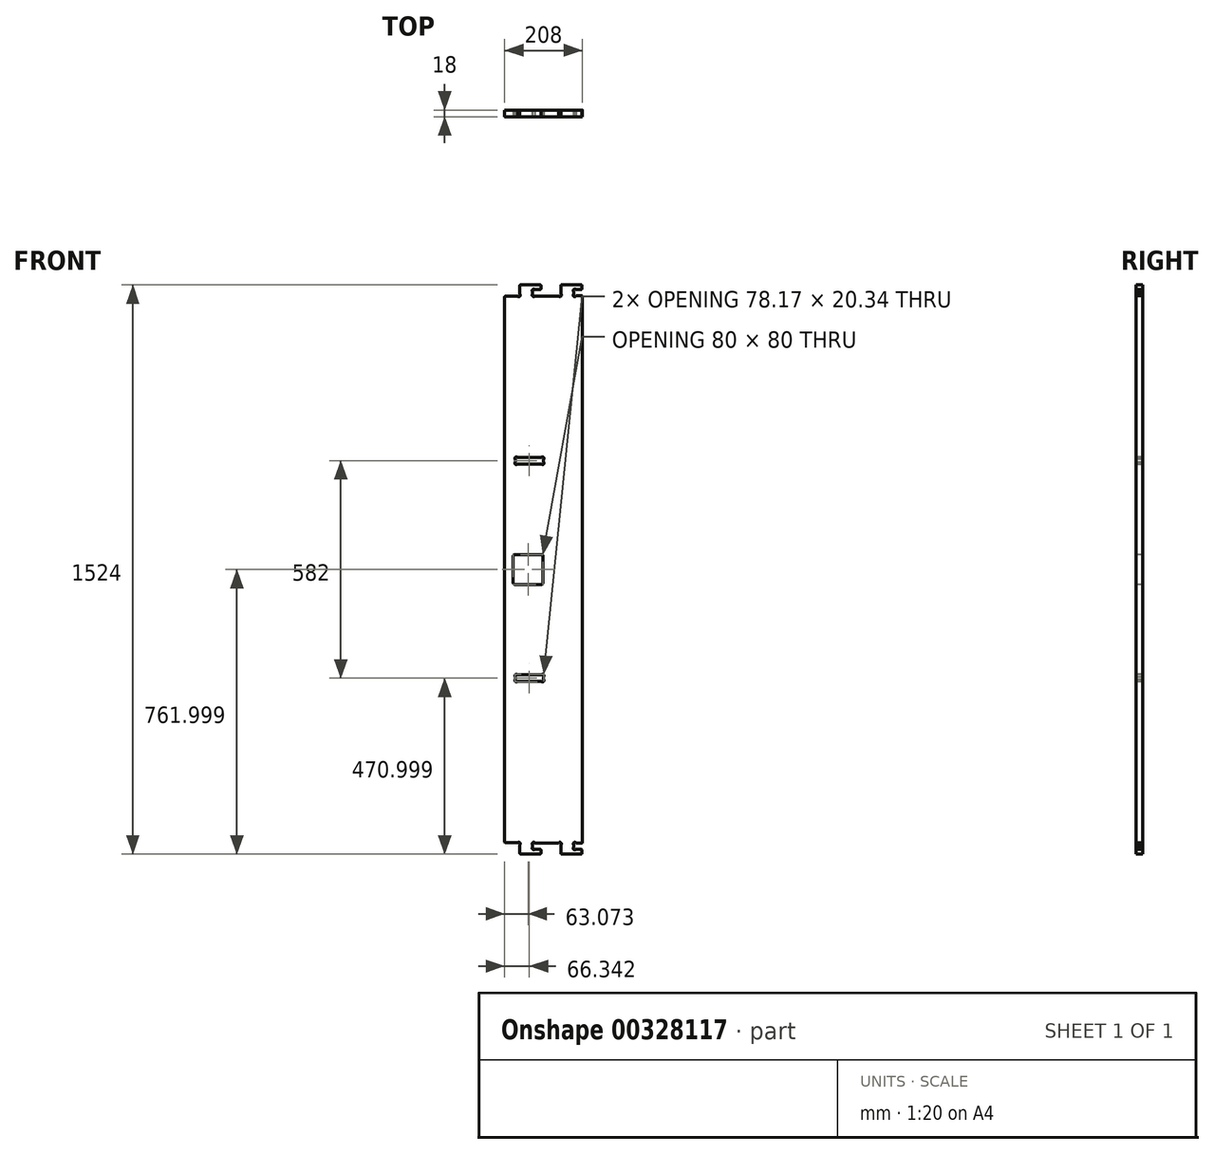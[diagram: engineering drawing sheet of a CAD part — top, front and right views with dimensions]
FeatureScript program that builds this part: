
annotation { "Feature Type Name" : "Feature", "Feature Type Description" : "" }
export const myFeature = defineFeature(function(context is Context, id is Id, definition is map)
    precondition{}
    {
        {
            var Q0;
            Q0=qCreatedBy(makeId("Front.planeOp"),FACE);
            var sketch = newSketch(context, id + "F0", { "sketchPlane" : qUnion([Q0])});
            skArc(sketch, "E0", {"start": v(-163.49, 53.85) * mm, "mid": v(-162.32, 56.68) * mm, "end": v(-159.49, 57.85) * mm});
            skLineSegment(sketch, "E1", {"start": v(-159.49, 57.85) * mm, "end": v(-87.49, 57.85) * mm});
            skArc(sketch, "E2", {"start": v(-87.49, 57.85) * mm, "mid": v(-84.66, 56.68) * mm, "end": v(-83.49, 53.85) * mm});
            skLineSegment(sketch, "E3", {"start": v(-83.49, 53.85) * mm, "end": v(-83.49, -18.15) * mm});
            skArc(sketch, "E4", {"start": v(-83.49, -18.15) * mm, "mid": v(-84.66, -20.98) * mm, "end": v(-87.49, -22.15) * mm});
            skLineSegment(sketch, "E5", {"start": v(-87.49, -22.15) * mm, "end": v(-159.49, -22.15) * mm});
            skArc(sketch, "E6", {"start": v(-159.49, -22.15) * mm, "mid": v(-162.32, -20.98) * mm, "end": v(-163.49, -18.15) * mm});
            skLineSegment(sketch, "E7", {"start": v(-163.49, -18.15) * mm, "end": v(-163.49, 53.85) * mm});
            skArc(sketch, "E8", {"start": v(-87.96, -282.15) * mm, "mid": v(-82.3, -282.15) * mm, "end": v(-82.3, -276.5) * mm});
            skLineSegment(sketch, "E9", {"start": v(-82.3, -276.5) * mm, "end": v(-82.3, -269.8) * mm});
            skArc(sketch, "E10", {"start": v(-82.3, -269.8) * mm, "mid": v(-82.3, -264.15) * mm, "end": v(-87.96, -264.15) * mm});
            skLineSegment(sketch, "E11", {"start": v(-87.96, -264.15) * mm, "end": v(-152.48, -264.15) * mm});
            skArc(sketch, "E12", {"start": v(-152.48, -264.15) * mm, "mid": v(-158.13, -264.15) * mm, "end": v(-158.13, -269.8) * mm});
            skLineSegment(sketch, "E13", {"start": v(-158.13, -269.8) * mm, "end": v(-158.13, -276.5) * mm});
            skArc(sketch, "E14", {"start": v(-158.13, -276.5) * mm, "mid": v(-158.13, -282.15) * mm, "end": v(-152.48, -282.15) * mm});
            skLineSegment(sketch, "E15", {"start": v(-152.48, -282.15) * mm, "end": v(-87.96, -282.15) * mm});
            skLineSegment(sketch, "E16", {"start": v(-82.3, 305.5) * mm, "end": v(-82.3, 312.2) * mm});
            skArc(sketch, "E17", {"start": v(-82.3, 312.2) * mm, "mid": v(-82.3, 317.85) * mm, "end": v(-87.96, 317.85) * mm});
            skLineSegment(sketch, "E18", {"start": v(-87.96, 317.85) * mm, "end": v(-152.48, 317.85) * mm});
            skArc(sketch, "E19", {"start": v(-152.48, 317.85) * mm, "mid": v(-158.13, 317.85) * mm, "end": v(-158.13, 312.2) * mm});
            skLineSegment(sketch, "E20", {"start": v(-158.13, 312.2) * mm, "end": v(-158.13, 305.5) * mm});
            skArc(sketch, "E21", {"start": v(-158.13, 305.5) * mm, "mid": v(-158.13, 299.85) * mm, "end": v(-152.48, 299.85) * mm});
            skLineSegment(sketch, "E22", {"start": v(-152.48, 299.85) * mm, "end": v(-87.96, 299.85) * mm});
            skArc(sketch, "E23", {"start": v(-87.96, 299.85) * mm, "mid": v(-82.3, 299.85) * mm, "end": v(-82.3, 305.5) * mm});
            skLineSegment(sketch, "E24", {"start": v(-105.9, -713.65) * mm, "end": v(-105.29, -714.15) * mm});
            skLineSegment(sketch, "E25", {"start": v(-105.29, -714.15) * mm, "end": v(-41.96, -714.15) * mm});
            skLineSegment(sketch, "E26", {"start": v(-41.96, -714.15) * mm, "end": v(-41.47, -713.65) * mm});
            skArc(sketch, "E27", {"start": v(-41.47, -713.65) * mm, "mid": v(-35.81, -713.65) * mm, "end": v(-35.81, -719.3) * mm});
            skLineSegment(sketch, "E28", {"start": v(-35.81, -719.3) * mm, "end": v(-35.8, -742.15) * mm});
            skArc(sketch, "E29", {"start": v(-35.8, -742.15) * mm, "mid": v(-35.22, -743.57) * mm, "end": v(-33.8, -744.15) * mm});
            skLineSegment(sketch, "E30", {"start": v(-33.8, -744.15) * mm, "end": v(18.44, -744.15) * mm});
            skArc(sketch, "E31", {"start": v(18.44, -744.15) * mm, "mid": v(19.85, -743.56) * mm, "end": v(20.44, -742.15) * mm});
            skLineSegment(sketch, "E32", {"start": v(20.44, -742.15) * mm, "end": v(20.44, -733.65) * mm});
            skArc(sketch, "E33", {"start": v(20.44, -733.65) * mm, "mid": v(19.85, -732.24) * mm, "end": v(18.44, -731.65) * mm});
            skLineSegment(sketch, "E34", {"start": v(18.44, -731.65) * mm, "end": v(4.1, -731.65) * mm});
            skArc(sketch, "E35", {"start": v(4.1, -731.65) * mm, "mid": v(-1.56, -731.65) * mm, "end": v(-1.56, -726) * mm});
            skLineSegment(sketch, "E36", {"start": v(-1.56, -726) * mm, "end": v(-1.56, -719.3) * mm});
            skArc(sketch, "E37", {"start": v(-1.56, -719.3) * mm, "mid": v(-1.56, -713.65) * mm, "end": v(4.1, -713.65) * mm});
            skLineSegment(sketch, "E38", {"start": v(4.1, -713.65) * mm, "end": v(5.07, -714.65) * mm});
            skLineSegment(sketch, "E39", {"start": v(5.07, -714.65) * mm, "end": v(20.44, -714.65) * mm});
            skArc(sketch, "E40", {"start": v(20.44, -714.65) * mm, "mid": v(21.14, -714.36) * mm, "end": v(21.44, -713.65) * mm});
            skLineSegment(sketch, "E41", {"start": v(21.44, -713.65) * mm, "end": v(21.44, 749.35) * mm});
            skArc(sketch, "E42", {"start": v(21.44, 749.35) * mm, "mid": v(21.14, 750.06) * mm, "end": v(20.44, 750.35) * mm});
            skLineSegment(sketch, "E43", {"start": v(20.44, 750.35) * mm, "end": v(5.12, 750.35) * mm});
            skLineSegment(sketch, "E44", {"start": v(5.12, 750.35) * mm, "end": v(4.1, 749.35) * mm});
            skArc(sketch, "E45", {"start": v(4.1, 749.35) * mm, "mid": v(-1.56, 749.35) * mm, "end": v(-1.56, 755) * mm});
            skLineSegment(sketch, "E46", {"start": v(-1.56, 755) * mm, "end": v(-1.56, 761.7) * mm});
            skArc(sketch, "E47", {"start": v(-1.56, 761.7) * mm, "mid": v(-1.56, 767.35) * mm, "end": v(4.1, 767.35) * mm});
            skLineSegment(sketch, "E48", {"start": v(4.1, 767.35) * mm, "end": v(18.44, 767.35) * mm});
            skArc(sketch, "E49", {"start": v(18.44, 767.35) * mm, "mid": v(19.85, 767.94) * mm, "end": v(20.44, 769.35) * mm});
            skLineSegment(sketch, "E50", {"start": v(20.44, 769.35) * mm, "end": v(20.44, 777.85) * mm});
            skArc(sketch, "E51", {"start": v(20.44, 777.85) * mm, "mid": v(19.85, 779.26) * mm, "end": v(18.44, 779.85) * mm});
            skLineSegment(sketch, "E52", {"start": v(18.44, 779.85) * mm, "end": v(-33.8, 779.85) * mm});
            skArc(sketch, "E53", {"start": v(-33.8, 779.85) * mm, "mid": v(-35.22, 779.26) * mm, "end": v(-35.8, 777.85) * mm});
            skLineSegment(sketch, "E54", {"start": v(-35.8, 777.85) * mm, "end": v(-35.81, 755) * mm});
            skArc(sketch, "E55", {"start": v(-35.81, 755) * mm, "mid": v(-35.81, 749.35) * mm, "end": v(-41.47, 749.35) * mm});
            skLineSegment(sketch, "E56", {"start": v(-41.47, 749.35) * mm, "end": v(-41.97, 749.85) * mm});
            skLineSegment(sketch, "E57", {"start": v(-41.97, 749.85) * mm, "end": v(-105.25, 749.85) * mm});
            skLineSegment(sketch, "E58", {"start": v(-105.25, 749.85) * mm, "end": v(-105.9, 749.35) * mm});
            skArc(sketch, "E59", {"start": v(-105.9, 749.35) * mm, "mid": v(-111.56, 749.35) * mm, "end": v(-111.56, 755) * mm});
            skLineSegment(sketch, "E60", {"start": v(-111.56, 755) * mm, "end": v(-111.56, 761.7) * mm});
            skArc(sketch, "E61", {"start": v(-111.56, 761.7) * mm, "mid": v(-111.56, 767.35) * mm, "end": v(-105.9, 767.35) * mm});
            skLineSegment(sketch, "E62", {"start": v(-105.9, 767.35) * mm, "end": v(-91.56, 767.35) * mm});
            skArc(sketch, "E63", {"start": v(-91.56, 767.35) * mm, "mid": v(-90.15, 767.94) * mm, "end": v(-89.56, 769.35) * mm});
            skLineSegment(sketch, "E64", {"start": v(-89.56, 769.35) * mm, "end": v(-89.56, 777.85) * mm});
            skArc(sketch, "E65", {"start": v(-89.56, 777.85) * mm, "mid": v(-90.15, 779.26) * mm, "end": v(-91.56, 779.85) * mm});
            skLineSegment(sketch, "E66", {"start": v(-91.56, 779.85) * mm, "end": v(-143.81, 779.85) * mm});
            skArc(sketch, "E67", {"start": v(-143.81, 779.85) * mm, "mid": v(-145.22, 779.26) * mm, "end": v(-145.81, 777.85) * mm});
            skLineSegment(sketch, "E68", {"start": v(-145.81, 777.85) * mm, "end": v(-145.81, 755) * mm});
            skArc(sketch, "E69", {"start": v(-145.81, 755) * mm, "mid": v(-145.81, 749.35) * mm, "end": v(-151.47, 749.35) * mm});
            skLineSegment(sketch, "E70", {"start": v(-151.47, 749.35) * mm, "end": v(-184.56, 749.35) * mm});
            skArc(sketch, "E71", {"start": v(-184.56, 749.35) * mm, "mid": v(-185.98, 748.76) * mm, "end": v(-186.56, 747.35) * mm});
            skLineSegment(sketch, "E72", {"start": v(-186.56, 747.35) * mm, "end": v(-186.56, -711.65) * mm});
            skArc(sketch, "E73", {"start": v(-186.56, -711.65) * mm, "mid": v(-185.98, -713.06) * mm, "end": v(-184.56, -713.65) * mm});
            skLineSegment(sketch, "E74", {"start": v(-184.56, -713.65) * mm, "end": v(-151.47, -713.65) * mm});
            skArc(sketch, "E75", {"start": v(-151.47, -713.65) * mm, "mid": v(-145.81, -713.65) * mm, "end": v(-145.81, -719.3) * mm});
            skLineSegment(sketch, "E76", {"start": v(-145.81, -719.3) * mm, "end": v(-145.81, -742.15) * mm});
            skArc(sketch, "E77", {"start": v(-145.81, -742.15) * mm, "mid": v(-145.22, -743.57) * mm, "end": v(-143.81, -744.15) * mm});
            skLineSegment(sketch, "E78", {"start": v(-143.81, -744.15) * mm, "end": v(-91.56, -744.15) * mm});
            skArc(sketch, "E79", {"start": v(-91.56, -744.15) * mm, "mid": v(-90.15, -743.56) * mm, "end": v(-89.56, -742.15) * mm});
            skLineSegment(sketch, "E80", {"start": v(-89.56, -742.15) * mm, "end": v(-89.56, -733.65) * mm});
            skArc(sketch, "E81", {"start": v(-89.56, -733.65) * mm, "mid": v(-90.15, -732.24) * mm, "end": v(-91.56, -731.65) * mm});
            skLineSegment(sketch, "E82", {"start": v(-91.56, -731.65) * mm, "end": v(-105.9, -731.65) * mm});
            skArc(sketch, "E83", {"start": v(-105.9, -731.65) * mm, "mid": v(-111.56, -731.65) * mm, "end": v(-111.56, -726) * mm});
            skLineSegment(sketch, "E84", {"start": v(-111.56, -726) * mm, "end": v(-111.56, -719.3) * mm});
            skArc(sketch, "E85", {"start": v(-111.56, -719.3) * mm, "mid": v(-111.56, -713.65) * mm, "end": v(-105.9, -713.65) * mm});
            skSolve(sketch);
        }
        {
            var Q0;
            Q0 = qSketchRegion(id + "F0", true);
            extrude(context, id + "F1", {"entities" : qUnion([Q0]), "oppositeDirection" : true, "depth" : 18 * mm});
        }
    });
